# Revit family: 50729003
name_source: partatom
category: Plumbing Fixtures
revit_build: Autodesk Revit 2017 (Build: 20190508_0315(x64)
units: mm (PartAtom-declared; Revit-internal decimal feet)

## family parameters
Always vertical = Yes
Cut with Voids When Loaded = No
OmniClass Number = 23.45.55.00
OmniClass Title = Sanitary Faucets, Wastes
Part Type = Normal
Room Calculation Point = No
Round Connector Dimension = Use Diameter
Shared = No
Work Plane-Based = No

## types (1)
- 50729003 Cover part for bath and shower faucet
    2D/3D/BIM Files URL = http://static.hansa.com
    AssetType = Fixed
    BIMObjectName = 50729003
    BodyMaterial = Brass
    Brand = Hansa
    Catalog Drawing URL = http://static.hansa.com
    Category = Bathroom
    Class = Single lever, Trim Kit
    CloseOffRating = 0
    Color = Chrome
    ConvergoRefNr = 0087-1909-0045-FI
    Customs Code = 84819000
    Dimension Drawing URL = http://static.hansa.com
    DurationUnit = Year
    EAN Number = 4057304012525
    EN Standard = EN 817
    FDV Document URL = http://www.hansa.com
    FaucetMainMaterial = Brass
    Features = Single lever, Trim Kit
    Finish = Polished
    FlowCoefficient = 0
    Group = Bath and shower faucets
    IfcExportAs = IfcValveType
    IfcExportType = FAUCET
    Installation Type = Wall mounted for concealed unit
    Installation and Maintenance = http://static.hansa.com
    Lever Handle = Single Operating Lever
    ManufacterURL = http://www.hansa.com
    Manufacturer = Hansa
    ManufacturerName = Hansa
    Material = Brass
    Max. Hot Water Supply = 80 °C
    Model = 50729003 Cover part for bath and shower faucet
    ModelReference = 50729003
    NBSDescription = Water supply fittings for baths
    NBSReference = 45-35-70/315
    Name = 50729003 Cover part for bath and shower faucet
    Name_en = 50729003 Cover part for bath and shower faucet
    NominalDepth = 90 mm
    NominalHeight = 167 mm
    NominalWidth = 130 mm
    Package Weight = 0.775 kg
    Package external Dimensions = 210 x 165 x 60
    Product Code = 50729003
    Product Datasheet = http://www.hansa.com
    Product Family = HANSADESIGNO
    Product Image URL = http://static.hansa.com
    Product URL = http://static.hansa.com
    Shape = Sculptured
    Size = 130x90x165 mm
    Spare Parts = http://static.hansa.com
    Uniclass2 = Pr_40_20_97_78
    Uniclass2015Description = Shower manual water supply sets
    Uniclass2015Reference = Pr_40_20_87_78
    Version = 1
    VersionDate = 17/07/2019
    WarrantyDescription = http://warranty.hansa.com
    WarrantyDurationUnit = Year
    WorkingPressure = 100 - 1000 kPa

## geometry (parser evidence)
native form markers: Sweep x5
no freeform markers — native parametric forms only
